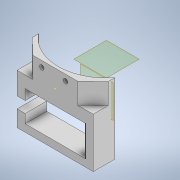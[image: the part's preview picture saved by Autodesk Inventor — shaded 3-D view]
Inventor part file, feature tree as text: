
AUTODESK INVENTOR PART (.ipt)
format: ipt  version: 2021 (Build 250183000, 183)  size: 203,264 bytes
history: native  units: mm
features: sketch x9, extrude x8, plane x2, other x1
ambient origin geometry x8: Origin, YZ Plane, XZ Plane, XY Plane, X Axis, Y Axis, Z Axis, Center Point
bodies: Body1 (feature_tree)
feature tree (20):
  other  "Sólido1"
  plane  "Plano de trabajo1"
  extrude  "Extrusión2"  Depth=3.0mm
  plane  "Plano de trabajo2"
  extrude  "Extrusión3"  Depth=2.0mm
  extrude  "Extrusión4"  Depth=50.0mm
  extrude  "Extrusión5"  Depth=15.0mm
  extrude  "Extrusión6"  Depth=15.0mm TaperAngle=0.0deg
  extrude  "Extrusión7"  Depth=8.0mm
  extrude  "Extrusión8"  Depth=3.0mm
  extrude  "Extrusión9"  Depth=12.0mm TaperAngle=0.0deg
  sketch  "Boceto11"  dims[d34=2.0mm d35=0.0mm d36=8.0mm d37=0.0mm d38=20.5mm d39=20.5mm d40=20.2mm d41=20.2mm d43=7.0mm d44=6.0mm d45=14.5mm d46=0.0mm d47=5.0mm d48=0.0mm d49=10.0mm d50=14.0mm d51=0.0mm d52=0.5mm d53=0.872665mm]
  sketch  "Boceto2"  dims[d15=3.0mm d16=3.0mm]
  sketch  "Boceto4"  dims[d17=12.0mm d18=0.0mm d19=2.0mm]
  sketch  "Boceto5"  dims[d20=20.0mm d21=50.0mm]
  sketch  "Boceto6"  dims[d22=100.0mm d23=15.0mm]
  sketch  "Boceto7"  dims[d24=15.0mm d25=12.0mm d26=0.0mm]
  sketch  "Boceto8"  dims[d27=8.0mm d28=8.0mm]
  sketch  "Boceto9"  dims[d29=16.0mm d30=3.0mm]
  sketch  "Boceto10"  dims[d31=3.0mm d32=12.0mm d33=0.0mm]
